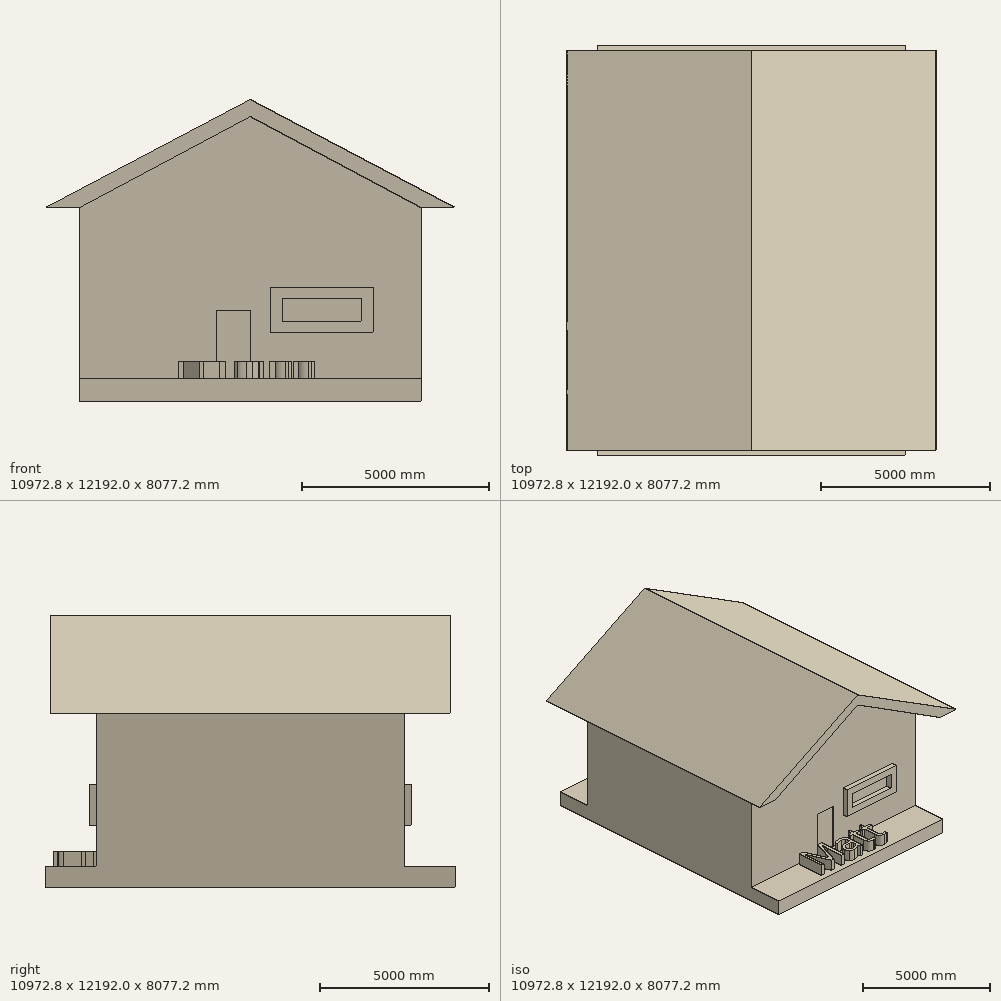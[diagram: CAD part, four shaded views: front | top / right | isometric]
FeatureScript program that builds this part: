
annotation { "Feature Type Name" : "Feature", "Feature Type Description" : "" }
export const myFeature = defineFeature(function(context is Context, id is Id, definition is map)
    precondition{}
    {
        {
            var Q0;
            Q0=qCreatedBy(makeId("Front.planeOp"),FACE);
            var sketch = newSketch(context, id + "F0", { "sketchPlane" : qUnion([Q0])});
            skLineSegment(sketch, "E0", {"start": v(0, 0) * mm, "end": v(-4572, 0) * mm});
            skLineSegment(sketch, "E1", {"start": v(0, 0) * mm, "end": v(4572, 0) * mm});
            skLineSegment(sketch, "E2", {"start": v(4572, 0) * mm, "end": v(4572, 4572) * mm});
            skLineSegment(sketch, "E3", {"start": v(4572, 4572) * mm, "end": v(-4572, 4572) * mm});
            skLineSegment(sketch, "E4", {"start": v(-4572, 4572) * mm, "end": v(-4572, 0) * mm});
            skLineSegment(sketch, "E5", {"start": v(-4572, 4572) * mm, "end": v(0, 7010.4) * mm});
            skLineSegment(sketch, "E6", {"start": v(4572, 4572) * mm, "end": v(0, 7010.4) * mm});
            skLineSegment(sketch, "E7", {"start": v(0, 0) * mm, "end": v(0, 1828.8) * mm});
            skLineSegment(sketch, "E8", {"start": v(0, 1828.8) * mm, "end": v(-914.4, 1828.8) * mm});
            skLineSegment(sketch, "E9", {"start": v(-914.4, 1828.8) * mm, "end": v(-914.4, 0) * mm});
            skLineSegment(sketch, "E10", {"start": v(-4572, 0) * mm, "end": v(-4572, -609.6) * mm});
            skLineSegment(sketch, "E11", {"start": v(-4572, -609.6) * mm, "end": v(4572, -609.6) * mm});
            skLineSegment(sketch, "E12.bottom", {"start": v(3286.6, 1231.1) * mm, "end": v(543.4, 1231.1) * mm});
            skLineSegment(sketch, "E12.top", {"start": v(3286.6, 2450.3) * mm, "end": v(543.4, 2450.3) * mm});
            skLineSegment(sketch, "E12.left", {"start": v(3286.6, 1231.1) * mm, "end": v(3286.6, 2450.3) * mm});
            skLineSegment(sketch, "E12.right", {"start": v(543.4, 1231.1) * mm, "end": v(543.4, 2450.3) * mm});
            skPoint(sketch, "E12.middle", {"position": v(1915, 1840.7) * mm});
            skLineSegment(sketch, "E13.bottom", {"start": v(2981.8, 1535.9) * mm, "end": v(848.2, 1535.9) * mm});
            skLineSegment(sketch, "E13.top", {"start": v(2981.8, 2145.5) * mm, "end": v(848.2, 2145.5) * mm});
            skLineSegment(sketch, "E13.left", {"start": v(2981.8, 1535.9) * mm, "end": v(2981.8, 2145.5) * mm});
            skLineSegment(sketch, "E13.right", {"start": v(848.2, 1535.9) * mm, "end": v(848.2, 2145.5) * mm});
            skLineSegment(sketch, "E14", {"start": v(-4572, 4572) * mm, "end": v(-5486.4, 4572) * mm});
            skLineSegment(sketch, "E15", {"start": v(4572, 4572) * mm, "end": v(5486.4, 4572) * mm});
            skLineSegment(sketch, "E16", {"start": v(0, 7010.4) * mm, "end": v(0, 7467.6) * mm});
            skLineSegment(sketch, "E17", {"start": v(0, 7467.6) * mm, "end": v(5486.4, 4572) * mm});
            skLineSegment(sketch, "E18", {"start": v(0, 7467.6) * mm, "end": v(-5486.4, 4572) * mm});
            skLineSegment(sketch, "E19", {"start": v(4572, 0) * mm, "end": v(4572, -609.6) * mm});
            skText(sketch, "E20", { "text": "Matt", "fontName": "OpenSans-Regular.ttf"});
            const initialGuessF0  = {"E20": [-3.48043, 7.74573, 1, 0, 2.64033]};
            skSetInitialGuess(sketch, initialGuessF0);
            skSolve(sketch);
        }
        {
            var Q0;
            Q0=makeQuery(id+"F0.imprint","IMPRINT",FACE,{"disambiguationData":[TD([[makeQuery(id+"F0.imprint","IMPRINT",EDGE,{"derivedFrom":sQuery(id+"F0.wireOp",EDGE,"E5")}),1.0]])]});
            var Q1;
            Q1=makeQuery(id+"F0.imprint","IMPRINT",FACE,{"disambiguationData":[TD([[makeQuery(id+"F0.imprint","IMPRINT",EDGE,{"derivedFrom":sQuery(id+"F0.wireOp",EDGE,"E6")}),-1.0]])]});
            extrude(context, id + "F1", {"entities" : qUnion([Q0, Q1]), "endBound" : BoundingType.SYMMETRIC, "depth" : 11887.2 * mm, "offsetDistance" : 30.48 * mm});
        }
        {
            var Q0;
            Q0=makeQuery(id+"F0.imprint","IMPRINT",FACE,{"disambiguationData":[TD([[makeQuery(id+"F0.imprint","IMPRINT",EDGE,{"derivedFrom":sQuery(id+"F0.wireOp",EDGE,"E3")}),-1.0]])]});
            extrude(context, id + "F2", {"entities" : qUnion([Q0]), "operationType" : NewBodyOperationType.ADD, "endBound" : BoundingType.SYMMETRIC, "depth" : 9144 * mm, "offsetDistance" : 30.48 * mm});
        }
        {
            var Q0;
            Q0=makeQuery(id+"F0.imprint","IMPRINT",FACE,{"disambiguationData":[TD([[makeQuery(id+"F0.imprint","IMPRINT",EDGE,{"derivedFrom":sQuery(id+"F0.wireOp",EDGE,"E1")}),1.0]])]});
            extrude(context, id + "F3", {"entities" : qUnion([Q0]), "operationType" : NewBodyOperationType.ADD, "endBound" : BoundingType.SYMMETRIC, "depth" : 9144 * mm, "offsetDistance" : 30.48 * mm});
        }
        {
            var Q0;
            {var subQ0=sQuery(id+"F0.wireOp",EDGE,"E7");Q0=makeQuery(id+"F0.imprint","IMPRINT",FACE,{"disambiguationData":[TD([[makeQuery(id+"F0.imprint","IMPRINT",EDGE,{"derivedFrom":subQ0}),1.0]])]});}
            extrude(context, id + "F4", {"entities" : qUnion([Q0]), "operationType" : NewBodyOperationType.ADD, "endBound" : BoundingType.SYMMETRIC, "depth" : 8991.6 * mm, "offsetDistance" : 30.48 * mm});
        }
        {
            var Q0;
            Q0=makeQuery(id+"F0.imprint","IMPRINT",FACE,{"disambiguationData":[TD([[makeQuery(id+"F0.imprint","IMPRINT",EDGE,{"derivedFrom":sQuery(id+"F0.wireOp",EDGE,"E12.bottom")}),-1.0]])]});
            extrude(context, id + "F5", {"entities" : qUnion([Q0]), "operationType" : NewBodyOperationType.ADD, "endBound" : BoundingType.SYMMETRIC, "depth" : 9601.2 * mm, "offsetDistance" : 30.48 * mm});
        }
        {
            var Q0;
            Q0=makeQuery(id+"F0.imprint","IMPRINT",FACE,{"disambiguationData":[TD([[makeQuery(id+"F0.imprint","IMPRINT",EDGE,{"derivedFrom":sQuery(id+"F0.wireOp",EDGE,"E13.bottom")}),-1.0]])]});
            extrude(context, id + "F6", {"entities" : qUnion([Q0]), "operationType" : NewBodyOperationType.ADD, "endBound" : BoundingType.SYMMETRIC, "depth" : 9144 * mm, "offsetDistance" : 30.48 * mm});
        }
        {
            var Q0;
            {var subQ0=sQuery(id+"F0.wireOp",EDGE,"E1");Q0=makeQuery(id+"F0.imprint","IMPRINT",FACE,{"disambiguationData":[TD([[makeQuery(id+"F0.imprint","IMPRINT",EDGE,{"derivedFrom":subQ0}),-1.0]])]});}
            extrude(context, id + "F7", {"entities" : qUnion([Q0]), "operationType" : NewBodyOperationType.ADD, "endBound" : BoundingType.SYMMETRIC, "depth" : 12192 * mm, "offsetDistance" : 30.48 * mm});
        }
        {
            var Q0;
            {var subQ6=sQuery(id+"F0.wireOp",EDGE,"E3");var subQ7=sQuery(id+"F0.wireOp",EDGE,"E1");var subQ8=sQuery(id+"F0.wireOp",EDGE,"E0");Q0=makeQuery(id+"F7.boolean.opBoolean","SPLIT",FACE,{"disambiguationData":[TD([makeQuery(id+"F2.opExtrude","CAP_FACE",FACE,{"disambiguationData":[OSD([subQ6,sQuery(id+"F0.wireOp",EDGE,"E5"),sQuery(id+"F0.wireOp",EDGE,"E6")])],"isStart":false})])],"derivedFrom":makeQuery(id+"F7.opExtrude","SWEPT_FACE",FACE,{"disambiguationData":[OSD([subQ8,subQ7])]})});}
            var sketch = newSketch(context, id + "F8", { "sketchPlane" : qUnion([Q0])});
            skText(sketch, "E21", { "text": "Matt", "fontName": "OpenSans-Regular.ttf"});
            const initialGuessF8  = {"E21": [-2.10702, -5.85542, 1, 0, 1.28342]};
            skSetInitialGuess(sketch, initialGuessF8);
            skSolve(sketch);
        }
        {
            var Q0;
            Q0 = qSketchRegion(id + "F8", true);
            extrude(context, id + "F9", {"entities" : qUnion([Q0]), "operationType" : NewBodyOperationType.ADD, "endBound" : BoundingType.SYMMETRIC, "depth" : 914.4 * mm, "offsetDistance" : 30.48 * mm});
        }
    });
